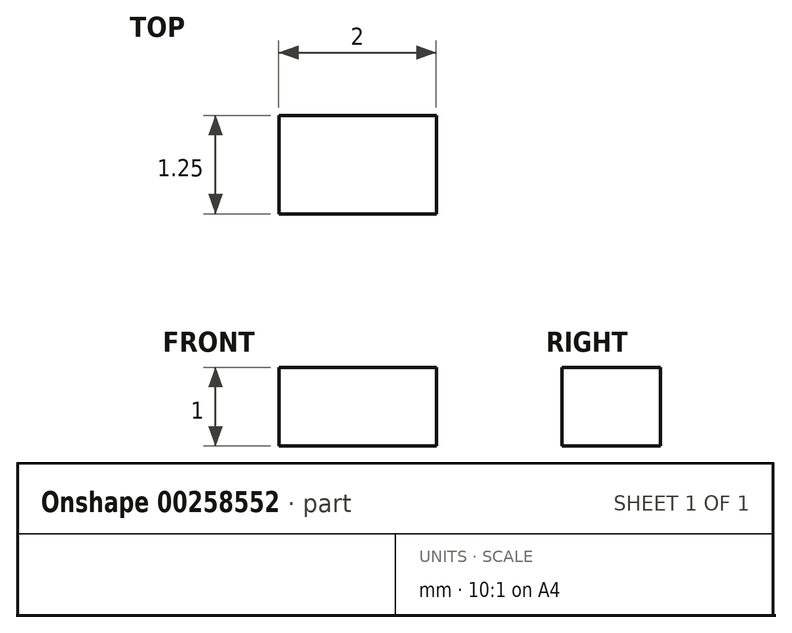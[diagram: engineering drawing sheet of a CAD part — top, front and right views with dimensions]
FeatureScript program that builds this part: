
annotation { "Feature Type Name" : "Feature", "Feature Type Description" : "" }
export const myFeature = defineFeature(function(context is Context, id is Id, definition is map)
    precondition{}
    {
        {
            var Q0;
            Q0=qCreatedBy(makeId("Top.planeOp"),FACE);
            var sketch = newSketch(context, id + "F0", { "sketchPlane" : qUnion([Q0])});
            skLineSegment(sketch, "E0.bottom", {"start": v(-0.27, 1.26) * mm, "end": v(1.73, 1.26) * mm});
            skLineSegment(sketch, "E0.top", {"start": v(-0.27, 0) * mm, "end": v(1.73, 0) * mm});
            skLineSegment(sketch, "E0.left", {"start": v(-0.27, 1.26) * mm, "end": v(-0.27, 0) * mm});
            skLineSegment(sketch, "E0.right", {"start": v(1.73, 1.26) * mm, "end": v(1.73, 0) * mm});
            skSolve(sketch);
        }
        {
            var Q0;
            Q0 = qSketchRegion(id + "F0", true);
            extrude(context, id + "F1", {"entities" : qUnion([Q0]), "depth" : 1 * mm});
        }
    });
